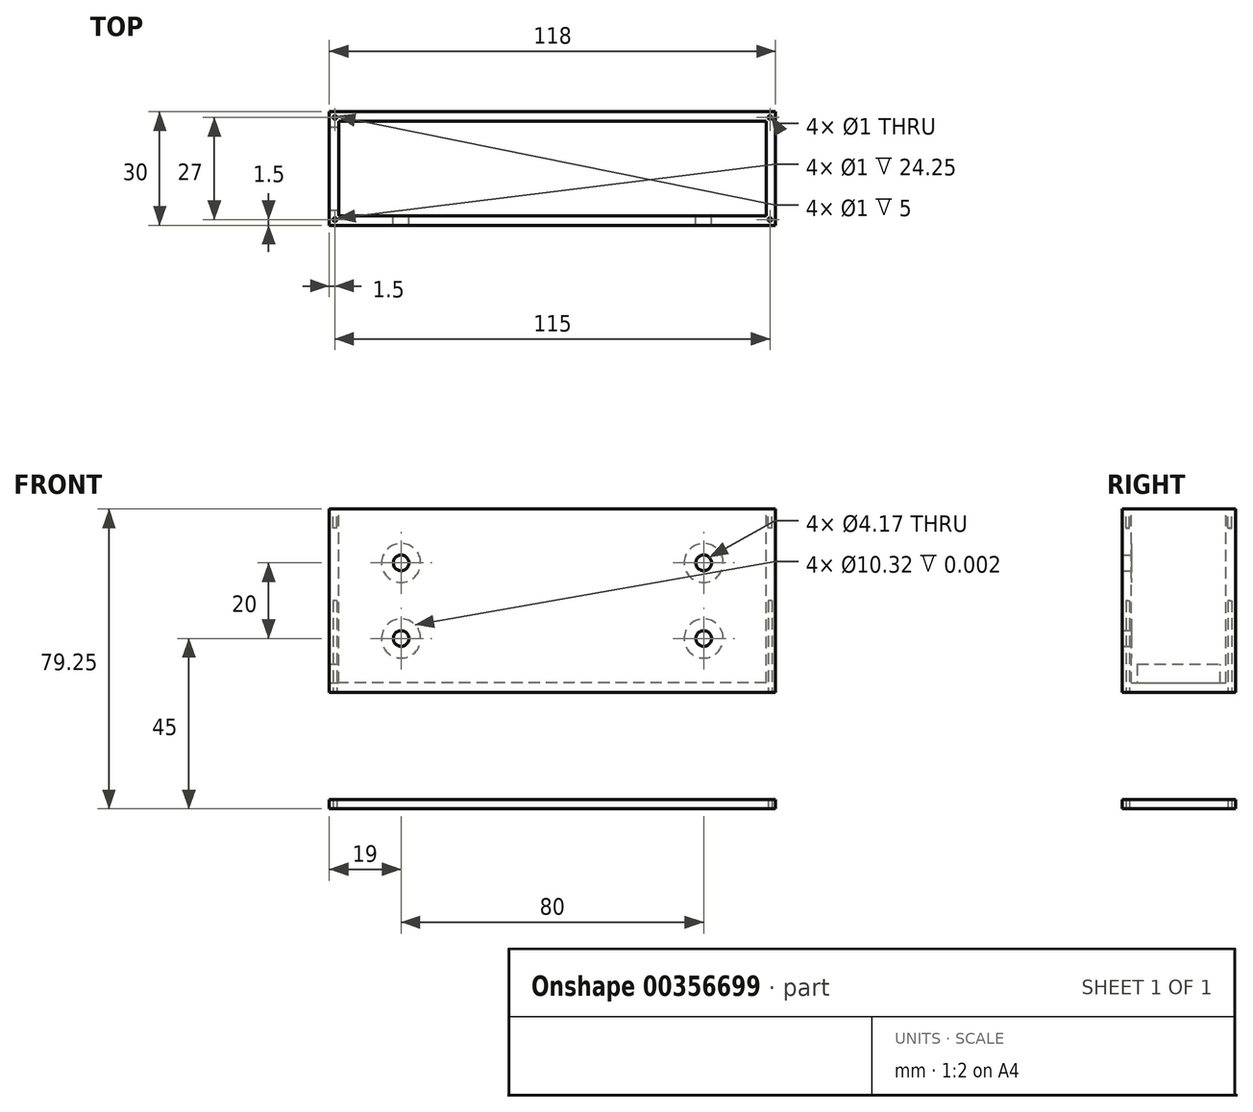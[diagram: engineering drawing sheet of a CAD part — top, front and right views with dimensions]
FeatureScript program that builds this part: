
annotation { "Feature Type Name" : "Feature", "Feature Type Description" : "" }
export const myFeature = defineFeature(function(context is Context, id is Id, definition is map)
    precondition{}
    {
        {
            var Q0;
            Q0=qCreatedBy(makeId("Front.planeOp"),FACE);
            var sketch = newSketch(context, id + "F0", { "sketchPlane" : qUnion([Q0])});
            skLineSegment(sketch, "E0.bottom", {"start": v(59, -24.25) * mm, "end": v(-59, -24.25) * mm});
            skLineSegment(sketch, "E0.top", {"start": v(59, 24.25) * mm, "end": v(-59, 24.25) * mm});
            skLineSegment(sketch, "E0.left", {"start": v(59, -24.25) * mm, "end": v(59, 24.25) * mm});
            skLineSegment(sketch, "E0.right", {"start": v(-59, -24.25) * mm, "end": v(-59, 24.25) * mm});
            skPoint(sketch, "E0.middle", {"position": v(0, 0) * mm});
            skSolve(sketch);
        }
        {
            var Q0;
            Q0=qSketchRegion(id+"F0",true);
            extrude(context, id + "F1", {"entities" : qUnion([Q0]), "endBound" : BoundingType.SYMMETRIC, "depth" : 30 * mm});
        }
        {
            var Q0;
            Q0=makeQuery(id+"F1.opExtrude","SWEPT_FACE",FACE,{"disambiguationData":[OSD([sQuery(id+"F0.wireOp",EDGE,"E0.top")])]});
            shell(context, id + "F2", {"entities" : qUnion([Q0]), "thickness" : 2.5 * mm});
        }
        {
            var Q0;
            Q0=qCreatedBy(makeId("Right.planeOp"),FACE);
            var sketch = newSketch(context, id + "F3", { "sketchPlane" : qUnion([Q0])});
            skLineSegment(sketch, "E1", {"start": v(11, -16.75) * mm, "end": v(11, -21.75) * mm});
            skLineSegment(sketch, "E2", {"start": v(11, -21.75) * mm, "end": v(-11, -21.75) * mm});
            skLineSegment(sketch, "E3", {"start": v(-11, -21.75) * mm, "end": v(-11, -16.75) * mm});
            skLineSegment(sketch, "E4", {"start": v(11, -16.75) * mm, "end": v(-11, -16.75) * mm});
            skSolve(sketch);
        }
        {
            var Q0;
            Q0=qSketchRegion(id+"F3",true);
            extrude(context, id + "F4", {"entities" : qUnion([Q0]), "operationType" : NewBodyOperationType.REMOVE, "oppositeDirection" : true, "depth" : 59.4 * mm});
        }
        {
            var Q0;
            Q0=qCreatedBy(makeId("Front.planeOp"),FACE);
            var sketch = newSketch(context, id + "F5", { "sketchPlane" : qUnion([Q0])});
            skCircle(sketch, "E5", {"center": v(40, -10) * mm, "radius": 2.08 * mm});
            skPoint(sketch, "E5.first.point", {"position": v(41.68, -8.77) * mm});
            skPoint(sketch, "E5.second.point", {"position": v(38.45, -11.4) * mm});
            skPoint(sketch, "E5.third.point", {"position": v(38.25, -8.87) * mm});
            skCircle(sketch, "E6", {"center": v(-40, -10) * mm, "radius": 2.08 * mm});
            skCircle(sketch, "E7", {"center": v(-40, 10) * mm, "radius": 2.08 * mm});
            skCircle(sketch, "E8", {"center": v(40, 10) * mm, "radius": 2.08 * mm});
            skSolve(sketch);
        }
        {
            var Q0;
            Q0=qSketchRegion(id+"F5",true);
            extrude(context, id + "F6", {"entities" : qUnion([Q0]), "operationType" : NewBodyOperationType.REMOVE, "depth" : 25 * mm});
        }
        {
            var Q0;
            Q0=qCreatedBy(makeId("Top.planeOp"),FACE);
            cPlane(context, id + "F7", {"entities" : qUnion([Q0]), "cplaneType" : CPlaneType.OFFSET, "offset" : 55 * mm, "oppositeDirection" : true, "width" : 150 * mm, "height" : 150 * mm});
        }
        {
            var Q0;
            Q0=qCreatedBy(id+"F7.planeOp",FACE);
            var sketch = newSketch(context, id + "F8", { "sketchPlane" : qUnion([Q0])});
            skLineSegment(sketch, "E9.bottom", {"start": v(59, -15) * mm, "end": v(-59, -15) * mm});
            skLineSegment(sketch, "E9.top", {"start": v(59, 15) * mm, "end": v(-59, 15) * mm});
            skLineSegment(sketch, "E9.left", {"start": v(59, -15) * mm, "end": v(59, 15) * mm});
            skLineSegment(sketch, "E9.right", {"start": v(-59, -15) * mm, "end": v(-59, 15) * mm});
            skPoint(sketch, "E9.middle", {"position": v(0, 0) * mm});
            skSolve(sketch);
        }
        {
            var Q0;
            Q0=qSketchRegion(id+"F8",true);
            extrude(context, id + "F9", {"entities" : qUnion([Q0]), "depth" : 2.5 * mm});
        }
        {
            var Q0;
            Q0=qCreatedBy(id+"F7.planeOp",FACE);
            var sketch = newSketch(context, id + "F10", { "sketchPlane" : qUnion([Q0])});
            skCircle(sketch, "E10", {"center": v(-57.5, 13.5) * mm, "radius": 0.5 * mm});
            skPoint(sketch, "E10.first.point", {"position": v(-57.94, 13.27) * mm});
            skPoint(sketch, "E10.second.point", {"position": v(-57.62, 13.01) * mm});
            skPoint(sketch, "E10.third.point", {"position": v(-57.16, 13.87) * mm});
            skCircle(sketch, "E11", {"center": v(-57.5, -13.5) * mm, "radius": 0.5 * mm});
            skCircle(sketch, "E12", {"center": v(57.5, -13.5) * mm, "radius": 0.5 * mm});
            skCircle(sketch, "E13", {"center": v(57.5, 13.5) * mm, "radius": 0.5 * mm});
            skSolve(sketch);
        }
        {
            var Q0;
            Q0=qSketchRegion(id+"F10",true);
            extrude(context, id + "F11", {"entities" : qUnion([Q0]), "operationType" : NewBodyOperationType.REMOVE, "depth" : 55 * mm});
        }
        {
            var Q0;
            Q0=makeQuery(id+"F1.opExtrude","SWEPT_FACE",FACE,{"disambiguationData":[OSD([sQuery(id+"F0.wireOp",EDGE,"E0.top")])]});
            var sketch = newSketch(context, id + "F12", { "sketchPlane" : qUnion([Q0])});
            skCircle(sketch, "E14", {"center": v(-57.5, 13.5) * mm, "radius": 0.5 * mm});
            skPoint(sketch, "E14.first.point", {"position": v(-58, 13.5) * mm});
            skPoint(sketch, "E14.second.point", {"position": v(-57.8, 13.1) * mm});
            skPoint(sketch, "E14.third.point", {"position": v(-57.46, 14) * mm});
            skCircle(sketch, "E15", {"center": v(-57.5, -13.5) * mm, "radius": 0.5 * mm});
            skCircle(sketch, "E16", {"center": v(57.5, -13.5) * mm, "radius": 0.5 * mm});
            skCircle(sketch, "E17", {"center": v(57.5, 13.5) * mm, "radius": 0.5 * mm});
            skSolve(sketch);
        }
        {
            var Q0;
            Q0=qSketchRegion(id+"F12",true);
            extrude(context, id + "F13", {"entities" : qUnion([Q0]), "operationType" : NewBodyOperationType.REMOVE, "oppositeDirection" : true, "depth" : 5 * mm});
        }
        {
            var Q0;
            {var subQ0=sQuery(id+"F0.wireOp",EDGE,"E0.right");var subQ1=sQuery(id+"F0.wireOp",EDGE,"E0.left");var subQ2=sQuery(id+"F0.wireOp",EDGE,"E0.top");var subQ3=sQuery(id+"F0.wireOp",EDGE,"E0.bottom");Q0=makeQuery(id+"F2.opShell","OFFSET_FACE",FACE,{"disambiguationData":[OSD([subQ3,subQ2,subQ1,subQ0]),TDD([makeQuery(id+"F1.opExtrude","CAP_FACE",FACE,{"disambiguationData":[OSD([subQ3,subQ2,subQ1,subQ0])],"isStart":false})])]});}
            var sketch = newSketch(context, id + "F14", { "sketchPlane" : qUnion([Q0])});
            skCircle(sketch, "E18", {"center": v(40, -10) * mm, "radius": 5.16 * mm});
            skCircle(sketch, "E19", {"center": v(40, 10) * mm, "radius": 5.16 * mm});
            skCircle(sketch, "E20", {"center": v(-40, 10) * mm, "radius": 5.16 * mm});
            skCircle(sketch, "E21", {"center": v(-40, -10) * mm, "radius": 5.16 * mm});
            skSolve(sketch);
        }
        {
            var Q0;
            Q0=qSketchRegion(id+"F14",true);
            extrude(context, id + "F15", {"entities" : qUnion([Q0]), "operationType" : NewBodyOperationType.REMOVE, "oppositeDirection" : true, "depth" : 1 / 406.4 * mm});
        }
    });
